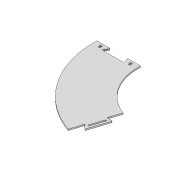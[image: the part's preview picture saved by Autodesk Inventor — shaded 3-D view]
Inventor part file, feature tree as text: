
AUTODESK INVENTOR PART (.ipt)
format: ipt  version: 2020 (Build 240168000, 168)  size: 240,640 bytes
history: native  units: mm
features: extrude x1, sketch x1
ambient origin geometry x8: Origin, YZ Plane, XZ Plane, XY Plane, X Axis, Y Axis, Z Axis, Center Point
bodies: Solid1 (feature_tree)
feature tree (2):
  extrude  "Extrusion1"  Depth=1.75mm
  sketch  "Sketch1"  dims[d0=504.787567mm d1=944.787567mm d2=50.0mm d4=360.0deg d6=7.5mm d7=7.5mm d9=68.5mm d10=7.5mm d11=7.5mm d12=3.5mm d13=3.5mm d17=50.0mm d19=360.0deg d21=4.363323mm d25=10.0mm d26=10.0mm d27=1.75mm d28=30.0mm d30=25.132741mm d32=7.0mm d33=0.0mm d34=0.0mm d35=8.0mm d36=1.75mm d38=50.0mm d40=50.0mm d42=30.0mm d43=8.0mm d44=1.75mm d45=50.0mm d47=360.0deg]
